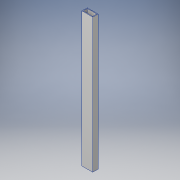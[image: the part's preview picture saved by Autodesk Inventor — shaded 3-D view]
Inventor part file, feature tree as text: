
AUTODESK INVENTOR PART (.ipt)
format: ipt  version: 2018 (Build 220112000, 112)  size: 109,568 bytes
history: native  units: in
note: dims shown in document units (in); Inventor stores cm internally (conversion verified against a paired STEP export)
features: extrude x2, sketch x2
ambient origin geometry x8: Origin, YZ Plane, XZ Plane, XY Plane, X Axis, Y Axis, Z Axis, Center Point
bodies: Solid1 (feature_tree)
feature tree (4):
  extrude  "Extrusion1"  Depth=2.0in
  extrude  "Extrusion2"  Depth=0.125in
  sketch  "Sketch1"  dims[d0=1.0in d1=2.0in]
  sketch  "Sketch2"  dims[d2=0.125in d3=0.125in d4=0.125in d5=0.125in d6=29.0in d7=0.0in d8=4.0in d9=0.0in]
